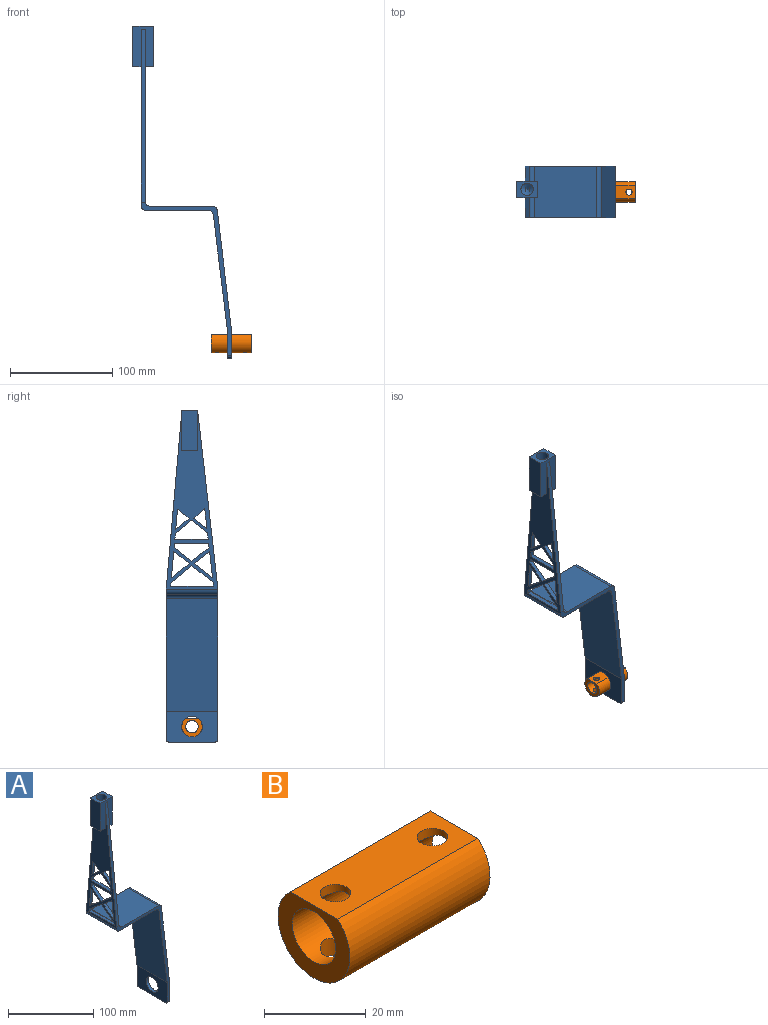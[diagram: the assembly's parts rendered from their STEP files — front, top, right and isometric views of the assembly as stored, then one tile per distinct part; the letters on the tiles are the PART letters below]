
ASSEMBLY  parts=2 mates=1
PART A: 57 faces, bbox 96x50x324.1 mm
  f0: plane 167.52x49.78mm, normal (1,0,0), area 3062.5mm2, adj f2,f13,f14,f15,f16,f17,f18,f19
  f1: plane 171.52x50mm, normal (-1,0,0), area 3215.4mm2, adj f2,f10,f11,f13,f14,f15,f16,f17
  f2: plane 168.41x19.19mm, normal (0,-0.99,0.11), area 678mm2, adj f0,f1,f10,f42,f49
  f3: plane 50x30mm, normal (1,0,0), area 1177.8mm2, adj f4,f9,f10,f11,f12,f46,f47
  f4: plane 113.73x50mm, normal (0.99,0,0.12), area 5726.5mm2, adj f3,f10,f11,f41
  f5: plane 60.56x50mm, normal (0,0,1), area 3027.9mm2, adj f10,f11,f41,f42
  f6: plane 60.58x50mm, normal (0,0,-1), area 3028.8mm2, adj f10,f11,f43,f44
  f7: plane 109.75x50mm, normal (-0.99,0,-0.12), area 5528.8mm2, adj f8,f10,f11,f44
  f8: plane 50x30mm, normal (-1,0,0), area 1177.8mm2, adj f7,f9,f10,f11,f12,f46,f47
  f9: plane 46x4mm, normal (0,0,-1), area 184mm2, adj f3,f8,f46,f47
  f10: plane 150.26x88.02mm, normal (0,-1,0), area 909mm2, adj f1,f2,f3,f4,f5,f6,f7,f8
  f11: plane 149.72x88.02mm, normal (0,1,0), area 906.8mm2, adj f1,f3,f4,f5,f6,f7,f8,f41
  f12: cylinder r=10.1mm len=20.2mm, axis (1,0,0), area 253.8mm2, adj f3,f8
  f13: plane 11.3x9.03mm, normal (0,0.62,-0.78), area 57.9mm2, adj f0,f1,f14,f15
  f14: plane 13.08x11.11mm, normal (0,0.65,0.76), area 68.6mm2, adj f0,f1,f13,f15
  f15: plane 20.15x4mm, normal (0,-1,-0.09), area 80.9mm2, adj f0,f1,f13,f14
  f16: plane 167.76x14.81mm, normal (0,1,0.09), area 673.7mm2, adj f0,f1,f42,f45,f51
  f17: plane 17.19x13.64mm, normal (0,-0.62,0.78), area 87.8mm2, adj f0,f1,f18,f21
  f18: plane 4.25x4mm, normal (0,-1,-0.09), area 17.1mm2, adj f0,f1,f17,f19
  f19: plane 33.29x4mm, normal (0,0,-1), area 133.2mm2, adj f0,f1,f18,f20
  f20: plane 4.16x4mm, normal (0,0.99,-0.11), area 16.7mm2, adj f0,f1,f19,f21
  f21: plane 16.95x13.74mm, normal (0,0.63,0.78), area 87.3mm2, adj f0,f1,f17,f20
  f22: plane 20.64x16.38mm, normal (0,0.62,-0.78), area 105.4mm2, adj f0,f1,f23,f26
  f23: plane 4.09x3.55mm, normal (0,0.99,-0.11), area 14.3mm2, adj f0,f1,f22,f24,f42
  f24: plane 41.79x4.18mm, normal (0,0.01,1), area 172.6mm2, adj f1,f23,f25,f42
  f25: plane 4.18x3.79mm, normal (0,-1,-0.09), area 15.3mm2, adj f0,f1,f24,f26,f42
  f26: plane 20.42x16.55mm, normal (0,-0.63,-0.78), area 105.1mm2, adj f0,f1,f22,f25
  f27: plane 19.24x4mm, normal (0,0.99,-0.11), area 77.5mm2, adj f0,f1,f28,f29
  f28: plane 12.89x10.15mm, normal (0,-0.62,0.79), area 65.6mm2, adj f0,f1,f27,f29
  f29: plane 10.7x9.09mm, normal (0,-0.65,-0.76), area 56.2mm2, adj f0,f1,f27,f28
  f30: plane 25.93x4mm, normal (0,0.99,-0.11), area 104.4mm2, adj f0,f1,f31,f32
  f31: plane 17.65x14.01mm, normal (0,-0.62,0.78), area 90.1mm2, adj f0,f1,f30,f32
  f32: plane 14.71x11.92mm, normal (0,-0.63,-0.78), area 75.7mm2, adj f0,f1,f30,f31
  f33: plane 15.72x12.57mm, normal (0,0.62,-0.78), area 80.5mm2, adj f0,f1,f34,f37
  f34: plane 5.93x4mm, normal (0,0.99,-0.11), area 23.9mm2, adj f0,f1,f33,f35
  f35: plane 32.52x4mm, normal (0,0.01,1), area 130.1mm2, adj f0,f1,f34,f36
  f36: plane 5.52x4mm, normal (0,-1,-0.09), area 22.2mm2, adj f0,f1,f35,f37
  f37: plane 15.64x13.29mm, normal (0,-0.65,-0.76), area 82.1mm2, adj f0,f1,f33,f36
  f38: plane 17.31x14.03mm, normal (0,0.63,0.78), area 89.1mm2, adj f0,f1,f39,f40
  f39: plane 25.96x4mm, normal (0,-1,-0.09), area 104.2mm2, adj f0,f1,f38,f40
  f40: plane 15.02x11.92mm, normal (0,0.62,-0.78), area 76.7mm2, adj f0,f1,f38,f39
  f41: cylinder r=5mm len=50mm, axis (0,-1,0), area 363.2mm2, adj f4,f5,f10,f11
  f42: cylinder r=5mm len=50mm, axis (0,-1,0), area 345.1mm2, adj f0,f2,f5,f10,f11,f16,f23,f24
  f43: cylinder r=5mm len=50mm, axis (0,1,0), area 392.7mm2, adj f1,f6,f10,f11
  f44: cylinder r=5mm len=50mm, axis (0,-1,0), area 362.2mm2, adj f6,f7,f10,f11
  f45: cylinder r=2mm len=4.21mm, axis (-1,0,0), area 0.7mm2, adj f1,f11,f16,f42
  f46: cylinder r=2mm len=4mm, axis (1,0,0), area 12.6mm2, adj f3,f8,f9,f11
  f47: cylinder r=2mm len=4mm, axis (-1,0,0), area 12.6mm2, adj f3,f8,f9,f10
  f48: plane 16x8mm, normal (0,0,-1), area 128mm2, adj f0,f49,f50,f51
  f49: plane 40x20mm, normal (0,-1,0), area 653.9mm2, adj f0,f1,f2,f48,f50,f52,f53,f54
  f50: plane 40x16mm, normal (1,0,0), area 640mm2, adj f48,f49,f51,f54
  f51: plane 40x20mm, normal (0,1,0), area 658mm2, adj f0,f1,f16,f48,f50,f52,f53,f54
  f52: plane 40x16mm, normal (-1,0,0), area 640mm2, adj f49,f51,f53,f54
  f53: plane 16x8mm, normal (0,0,-1), area 128mm2, adj f1,f49,f51,f52
  f54: plane 20x16mm, normal (0,0,1), area 206.9mm2, adj f49,f50,f51,f52,f55
  f55: cylinder r=6mm len=37mm, axis (0,0,1), area 1394.9mm2, adj f54,f56
  f56: cone r=0mm half-angle=59deg, axis (0,0,1), area 131.9mm2, adj f55
PART B: 9 faces, bbox 39x20x17.5 mm
  f0: cylinder r=6.05mm len=39mm, axis (-1,0,0), area 1365.5mm2, adj f3,f4,f5,f6,f7,f8
  f1: cylinder r=10mm len=39mm, axis (-1,0,0), area 1829.5mm2, adj f2,f3,f4,f5,f7
  f2: plane 39x13.23mm, normal (0,0,1), area 459.4mm2, adj f1,f3,f4,f6,f8
  f3: plane 20x17.5mm, normal (1,0,0), area 176.5mm2, adj f0,f1,f2
  f4: plane 20x17.5mm, normal (-1,0,0), area 176.5mm2, adj f0,f1,f2
  f5: cylinder r=3mm len=6mm, axis (0,0,1), area 77.5mm2, adj f0,f1
  f6: cylinder r=3mm len=6mm, axis (0,0,1), area 34.7mm2, adj f0,f2
  f7: cylinder r=3mm len=6mm, axis (0,0,1), area 77.5mm2, adj f0,f1
  f8: cylinder r=3mm len=6mm, axis (0,0,1), area 34.7mm2, adj f0,f2
PLACE A t=(-62.45,-19.31,-139.81)mm
PLACE B t=(-77.95,-44.31,-124.81)mm
MATE revolute B.f0 <-> A.f12  axis (-1,0,0) through (-58.45,-44.31,-124.81)mm
